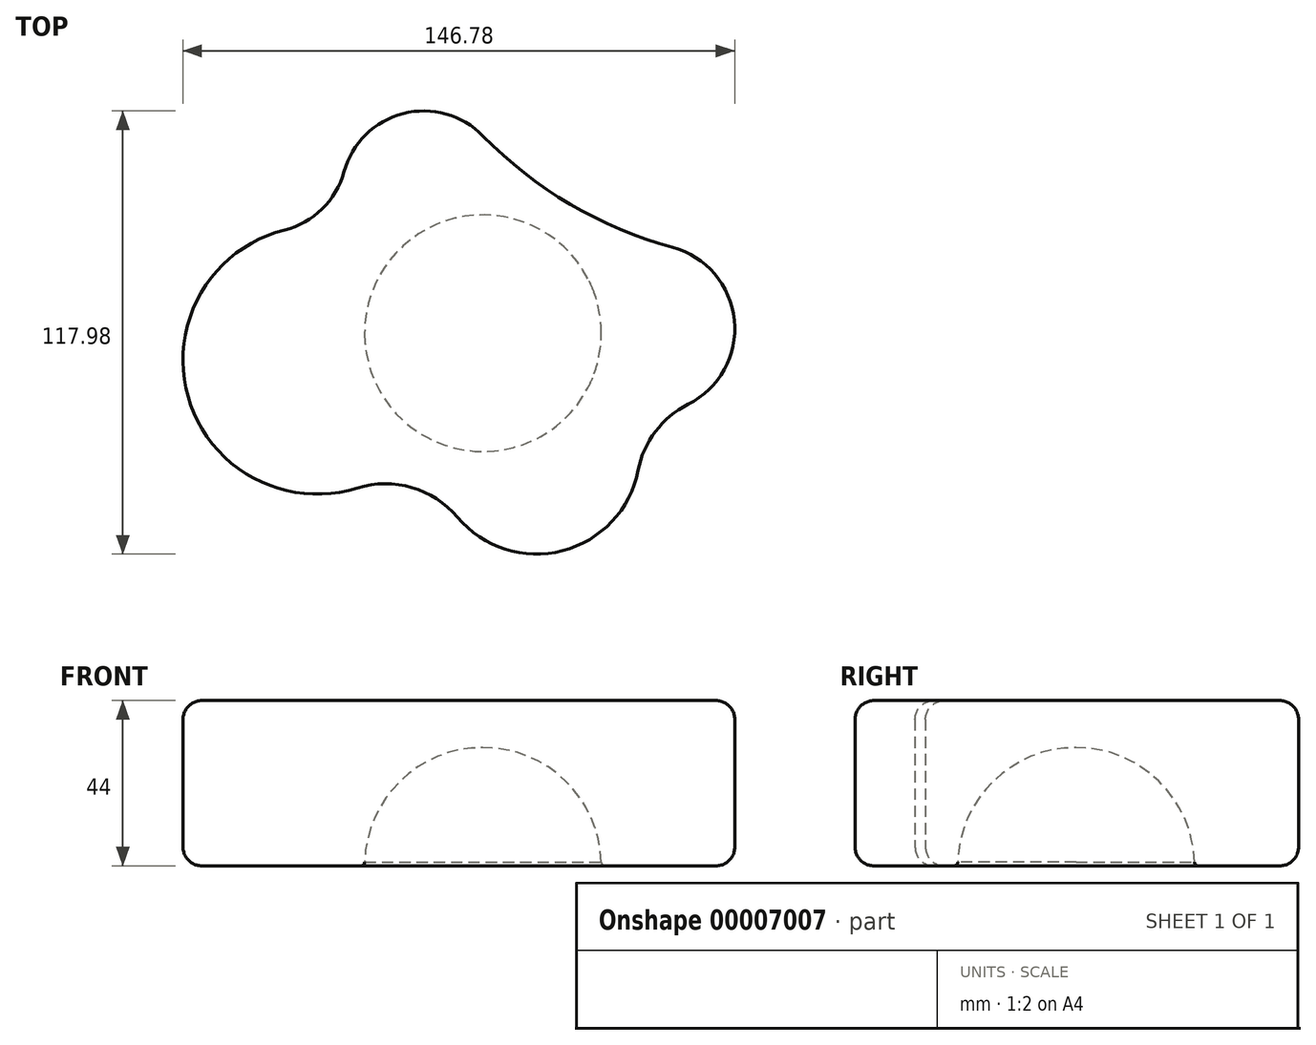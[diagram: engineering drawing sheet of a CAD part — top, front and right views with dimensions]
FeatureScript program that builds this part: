
annotation { "Feature Type Name" : "Feature", "Feature Type Description" : "" }
export const myFeature = defineFeature(function(context is Context, id is Id, definition is map)
    precondition{}
    {
        {
            var Q0;
            Q0=qCreatedBy(makeId("Top.planeOp"),FACE);
            var sketch = newSketch(context, id + "F0", { "sketchPlane" : qUnion([Q0])});
            skArc(sketch, "E0", {"start": v(-6.78, -48.98) * mm, "mid": v(21.17, -57.91) * mm, "end": v(41.25, -36.53) * mm});
            skArc(sketch, "E1", {"start": v(-52.82, 27.46) * mm, "mid": v(-78.45, -16.86) * mm, "end": v(-33.41, -41.2) * mm});
            skArc(sketch, "E2", {"start": v(54.58, -18.93) * mm, "mid": v(66.87, 3.45) * mm, "end": v(50.37, 22.93) * mm});
            skArc(sketch, "E3", {"start": v(0, 52.54) * mm, "mid": v(23.2, 34.36) * mm, "end": v(50.37, 22.93) * mm});
            skPoint(sketch, "E4.visualSharp", {"position": v(-11.12, -20.8) * mm});
            skArc(sketch, "E4.filletArc", {"start": v(-6.78, -48.98) * mm, "mid": v(-18.92, -41.06) * mm, "end": v(-33.41, -41.2) * mm});
            skPoint(sketch, "E5.visualSharp", {"position": v(39.66, -20.8) * mm});
            skArc(sketch, "E5.filletArc", {"start": v(54.58, -18.93) * mm, "mid": v(45.87, -26.18) * mm, "end": v(41.25, -36.53) * mm});
            skPoint(sketch, "E6.newPointA", {"position": v(0, 207.56) * mm});
            skArc(sketch, "E6.filletArc", {"start": v(0, 52.54) * mm, "mid": v(-21.25, 58.48) * mm, "end": v(-36.97, 42.99) * mm});
            skArc(sketch, "E7.filletArc", {"start": v(-52.82, 27.46) * mm, "mid": v(-42.8, 33.08) * mm, "end": v(-36.97, 42.99) * mm});
            skSolve(sketch);
        }
        {
            var Q0;
            Q0 = qSketchRegion(id + "F0", true);
            extrude(context, id + "F1", {"entities" : qUnion([Q0]), "depth" : 44 * mm});
        }
        {
            var Q0;
            Q0=qCreatedBy(makeId("Front.planeOp"),FACE);
            var sketch = newSketch(context, id + "F2", { "sketchPlane" : qUnion([Q0])});
            skArc(sketch, "E8", {"start": v(31.5, 0) * mm, "mid": v(0, 31.5) * mm, "end": v(-31.5, 0) * mm});
            skLineSegment(sketch, "E9", {"start": v(0, 0) * mm, "end": v(132.89, 0) * mm, "construction": true});
            skLineSegment(sketch, "E10", {"start": v(0, 0) * mm, "end": v(-143.59, 0) * mm, "construction": true});
            skLineSegment(sketch, "E11", {"start": v(-31.5, 0) * mm, "end": v(31.5, 0) * mm});
            skSolve(sketch);
        }
        {
            var Q0;
            Q0 = qSketchRegion(id + "F2", true);
            var Q1;
            Q1=sQuery(id+"F2.wireOp",EDGE,"E9");
            revolve(context, id + "F3", {"operationType" : NewBodyOperationType.REMOVE, "entities" : qUnion([Q0]), "axis" : qUnion([Q1]), "revolveType" : RevolveType.FULL, "oppositeDirection" : true});
        }
        {
            var Q0;
            Q0=makeQuery(id+"F3.boolean.opBoolean","INTERSECT",EDGE,{"derivedFrom":[makeQuery(id+"F1.opExtrude","CAP_FACE",FACE,{"disambiguationData":[OSD([sQuery(id+"F0.wireOp",EDGE,"E0"),sQuery(id+"F0.wireOp",EDGE,"E1"),sQuery(id+"F0.wireOp",EDGE,"E2"),sQuery(id+"F0.wireOp",EDGE,"E3"),sQuery(id+"F0.wireOp",EDGE,"E4.filletArc"),sQuery(id+"F0.wireOp",EDGE,"E5.filletArc"),sQuery(id+"F0.wireOp",EDGE,"E6.filletArc"),sQuery(id+"F0.wireOp",EDGE,"E7.filletArc")])],"isStart":true}),makeQuery(id+"F3.opRevolve","SWEPT_FACE",FACE,{"disambiguationData":[OSD([sQuery(id+"F2.wireOp",EDGE,"E8")])]})]});
            fillet(context, id + "F4", {"entities" : qUnion([Q0]), "radius" : 1 * mm, "tangentPropagation" : true, "allowEdgeOverflow" : false});
        }
        {
            var Q0;
            Q0=makeQuery(id+"F1.opExtrude","SWEPT_FACE",FACE,{"disambiguationData":[OSD([sQuery(id+"F0.wireOp",EDGE,"E6.filletArc")])]});
            fillet(context, id + "F5", {"entities" : qUnion([Q0]), "radius" : 5 * mm, "tangentPropagation" : true, "allowEdgeOverflow" : false});
        }
    });
